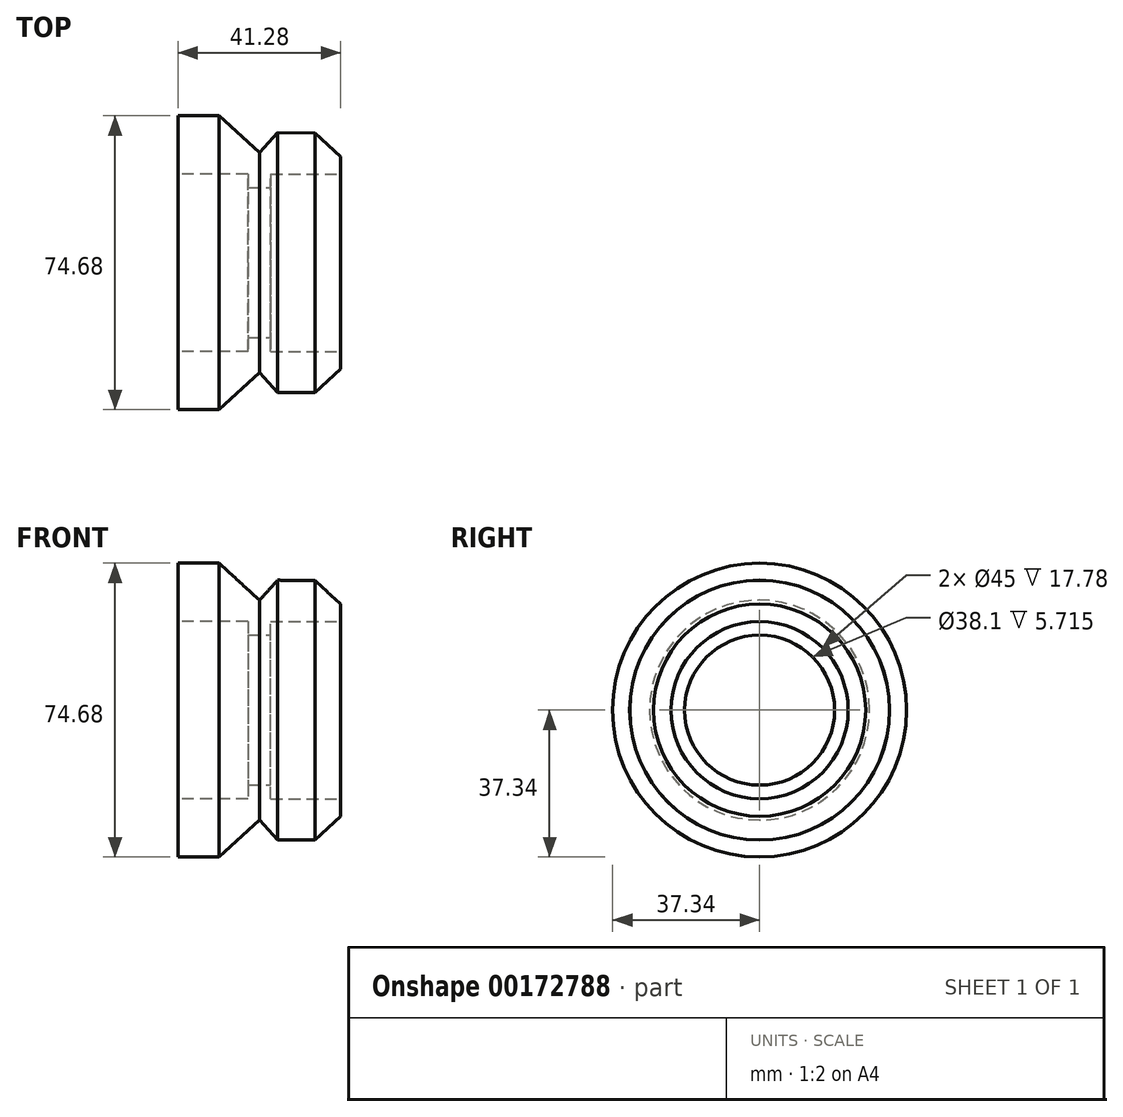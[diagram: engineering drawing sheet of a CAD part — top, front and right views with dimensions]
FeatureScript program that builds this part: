
annotation { "Feature Type Name" : "Feature", "Feature Type Description" : "" }
export const myFeature = defineFeature(function(context is Context, id is Id, definition is map)
    precondition{}
    {
        {
            var Q0;
            Q0=qCreatedBy(makeId("Right.planeOp"),FACE);
            var sketch = newSketch(context, id + "F0", { "sketchPlane" : qUnion([Q0])});
            skCircle(sketch, "E0", {"center": v(0, 0) * mm, "radius": 23.5 * mm});
            skSolve(sketch);
        }
        {
            var Q0;
            Q0=qCreatedBy(makeId("Front.planeOp"),FACE);
            var sketch = newSketch(context, id + "F1", { "sketchPlane" : qUnion([Q0])});
            skLineSegment(sketch, "E1", {"start": v(0, 25.4) * mm, "end": v(-20.64, 25.4) * mm});
            skLineSegment(sketch, "E2", {"start": v(-20.64, 25.4) * mm, "end": v(-20.64, 37.34) * mm});
            skLineSegment(sketch, "E3", {"start": v(0, 25.4) * mm, "end": v(20.64, 25.4) * mm});
            skLineSegment(sketch, "E4", {"start": v(20.64, 25.4) * mm, "end": v(20.64, 26.96) * mm});
            skLineSegment(sketch, "E5", {"start": v(-10.18, 37.34) * mm, "end": v(-20.64, 37.34) * mm});
            skLineSegment(sketch, "E6", {"start": v(4.69, 33.02) * mm, "end": v(14.1, 32.99) * mm});
            skLineSegment(sketch, "E7", {"start": v(0, 27.94) * mm, "end": v(-10.18, 37.34) * mm});
            skLineSegment(sketch, "E8", {"start": v(0, 27.94) * mm, "end": v(4.69, 33.02) * mm});
            skLineSegment(sketch, "E9", {"start": v(20.64, 26.96) * mm, "end": v(14.1, 32.99) * mm});
            skSolve(sketch);
        }
        {
            var Q0;
            Q0=makeQuery(id+"F1.imprint","IMPRINT",FACE,{"disambiguationData":[TD([[makeQuery(id+"F1.imprint","IMPRINT",EDGE,{"derivedFrom":sQuery(id+"F1.wireOp",EDGE,"E1")}),-1.0]])]});
            var Q1;
            Q1=sQuery(id+"F0.wireOp",EDGE,"E0");
            revolve(context, id + "F2", {"entities" : qUnion([Q0]), "axis" : qUnion([Q1]), "revolveType" : RevolveType.FULL});
        }
        {
            var Q0;
            Q0=makeQuery(id+"F2.opRevolve","SWEPT_FACE",FACE,{"disambiguationData":[OSD([sQuery(id+"F1.wireOp",EDGE,"E4")])]});
            var sketch = newSketch(context, id + "F3", { "sketchPlane" : qUnion([Q0])});
            skCircle(sketch, "E10", {"center": v(0, 0) * mm, "radius": 24.8 * mm});
            skSolve(sketch);
        }
        {
            var Q0;
            Q0=makeQuery(id+"F3.imprint","IMPRINT",FACE,{"disambiguationData":[TD([[makeQuery(id+"F3.imprint","IMPRINT",EDGE,{"derivedFrom":makeQuery(id+"F2.opRevolve","SWEPT_EDGE",EDGE,{"disambiguationData":[OSD([sQuery(id+"F1.wireOp",EDGE,"E3"),sQuery(id+"F1.wireOp",EDGE,"E4")])]})}),-1.0]])]});
            var Q1;
            Q1=makeQuery(id+"F2.opRevolve","SWEPT_FACE",FACE,{"disambiguationData":[OSD([sQuery(id+"F1.wireOp",EDGE,"E2")])]});
            extrude(context, id + "F4", {"entities" : qUnion([Q0]), "operationType" : NewBodyOperationType.ADD, "endBound" : BoundingType.UP_TO_SURFACE, "oppositeDirection" : true, "endBoundEntityFace" : qUnion([Q1]), "depth" : 25.4 * mm});
        }
        {
            var Q0;
            {var subQ0=sQuery(id+"F1.wireOp",EDGE,"E4");Q0=makeQuery(id+"F4.boolean.opBoolean","MERGE",FACE,{"derivedFrom":[makeQuery(id+"F2.opRevolve","SWEPT_FACE",FACE,{"disambiguationData":[OSD([subQ0])]}),makeQuery(id+"F4.opExtrude","CAP_FACE",FACE,{"disambiguationData":[OSD([sQuery(id+"F1.wireOp",EDGE,"E3"),subQ0])],"isStart":true})]});}
            var sketch = newSketch(context, id + "F5", { "sketchPlane" : qUnion([Q0])});
            skCircle(sketch, "E11", {"center": v(0, 0) * mm, "radius": 19.05 * mm});
            skSolve(sketch);
        }
        {
            var Q0;
            Q0=makeQuery(id+"F5.imprint","IMPRINT",FACE,{"disambiguationData":[TD([[makeQuery(id+"F5.imprint","IMPRINT",EDGE,{"derivedFrom":sQuery(id+"F5.wireOp",EDGE,"E11")}),1.0]])]});
            extrude(context, id + "F6", {"entities" : qUnion([Q0]), "operationType" : NewBodyOperationType.REMOVE, "endBound" : BoundingType.THROUGH_ALL, "oppositeDirection" : true, "depth" : 25.4 * mm});
        }
        {
            var Q0;
            Q0 = qSketchRegion(id + "F3", true);
            var Q1;
            {var subQ0=sQuery(id+"F1.wireOp",EDGE,"E2");Q1=makeQuery(id+"F4.boolean.opBoolean","MERGE",FACE,{"derivedFrom":[makeQuery(id+"F2.opRevolve","SWEPT_FACE",FACE,{"disambiguationData":[OSD([subQ0])]}),makeQuery(id+"F4.opExtrude","CAP_FACE",FACE,{"disambiguationData":[OSD([subQ0])],"isStart":false})]});}
            extrude(context, id + "F7", {"entities" : qUnion([Q0]), "operationType" : NewBodyOperationType.ADD, "endBound" : BoundingType.UP_TO_SURFACE, "oppositeDirection" : true, "endBoundEntityFace" : qUnion([Q1]), "depth" : 25.4 * mm});
        }
        {
            var Q0;
            Q0 = qSketchRegion(id + "F5", true);
            extrude(context, id + "F8", {"entities" : qUnion([Q0]), "operationType" : NewBodyOperationType.REMOVE, "endBound" : BoundingType.THROUGH_ALL, "oppositeDirection" : true, "depth" : 25.4 * mm});
        }
        {
            var Q0;
            {var subQ0=sQuery(id+"F3.wireOp",EDGE,"E10");var subQ1=sQuery(id+"F1.wireOp",EDGE,"E4");Q0=makeQuery(id+"F7.boolean.opBoolean","MERGE",FACE,{"derivedFrom":[makeQuery(id+"F4.boolean.opBoolean","MERGE",FACE,{"derivedFrom":[makeQuery(id+"F2.opRevolve","SWEPT_FACE",FACE,{"disambiguationData":[OSD([subQ1])]}),makeQuery(id+"F4.opExtrude","CAP_FACE",FACE,{"disambiguationData":[OSD([sQuery(id+"F1.wireOp",EDGE,"E3"),subQ1,subQ0])],"isStart":true})]}),makeQuery(id+"F7.opExtrude","CAP_FACE",FACE,{"disambiguationData":[OSD([subQ0])],"isStart":true})]});}
            var sketch = newSketch(context, id + "F9", { "sketchPlane" : qUnion([Q0])});
            skCircle(sketch, "E12", {"center": v(0, 0) * mm, "radius": 22.5 * mm});
            skSolve(sketch);
        }
        {
            var Q0;
            Q0=makeQuery(id+"F9.imprint","IMPRINT",FACE,{"disambiguationData":[TD([[makeQuery(id+"F9.imprint","IMPRINT",EDGE,{"derivedFrom":sQuery(id+"F9.wireOp",EDGE,"E12")}),1.0]])]});
            extrude(context, id + "F10", {"entities" : qUnion([Q0]), "operationType" : NewBodyOperationType.REMOVE, "oppositeDirection" : true, "depth" : 17.78 * mm});
        }
        {
            var Q0;
            {var subQ0=sQuery(id+"F1.wireOp",EDGE,"E2");Q0=makeQuery(id+"F7.boolean.opBoolean","MERGE",FACE,{"derivedFrom":[makeQuery(id+"F4.boolean.opBoolean","MERGE",FACE,{"derivedFrom":[makeQuery(id+"F2.opRevolve","SWEPT_FACE",FACE,{"disambiguationData":[OSD([subQ0])]}),makeQuery(id+"F4.opExtrude","CAP_FACE",FACE,{"disambiguationData":[OSD([subQ0])],"isStart":false})]}),makeQuery(id+"F7.opExtrude","CAP_FACE",FACE,{"disambiguationData":[OSD([subQ0])],"isStart":false})]});}
            var sketch = newSketch(context, id + "F11", { "sketchPlane" : qUnion([Q0])});
            skCircle(sketch, "E13", {"center": v(0, 0) * mm, "radius": 22.5 * mm});
            skSolve(sketch);
        }
        {
            var Q0;
            Q0=makeQuery(id+"F11.imprint","IMPRINT",FACE,{"disambiguationData":[TD([[makeQuery(id+"F11.imprint","IMPRINT",EDGE,{"derivedFrom":sQuery(id+"F11.wireOp",EDGE,"E13")}),1.0]])]});
            extrude(context, id + "F12", {"entities" : qUnion([Q0]), "operationType" : NewBodyOperationType.REMOVE, "oppositeDirection" : true, "depth" : 17.78 * mm});
        }
    });
